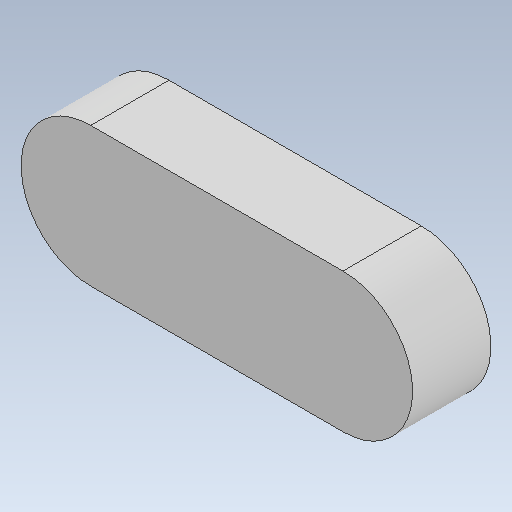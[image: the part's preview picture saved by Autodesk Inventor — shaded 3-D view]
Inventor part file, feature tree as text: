
AUTODESK INVENTOR PART (.ipt)
format: ipt  version: 2020 (Build 240168000, 168)  size: 89,600 bytes
history: native  units: mm
features: other x2, extrude x1, sketch x1, reference x1
ambient origin geometry x8: Origin, YZ Plane, XZ Plane, XY Plane, X Axis, Y Axis, Z Axis, Center Point
bodies: 实体1 (feature_tree)
feature tree (5):
  extrude  "拉伸1"  [1 undecoded]
  sketch  "草图1"  dims[d0=18.0mm d1=0.0mm]
  reference  "参考1"
  other  "<userpath>\Desktop\ME_course_project\课设试试\shaft_try_1.iam"
  other  "shaft_try_1.iam"
note: 1 required parameter value undecoded (feature->parameter linkage not recoverable at this tier; creation-order binding heuristic only, values carry confidence <= 0.55)
